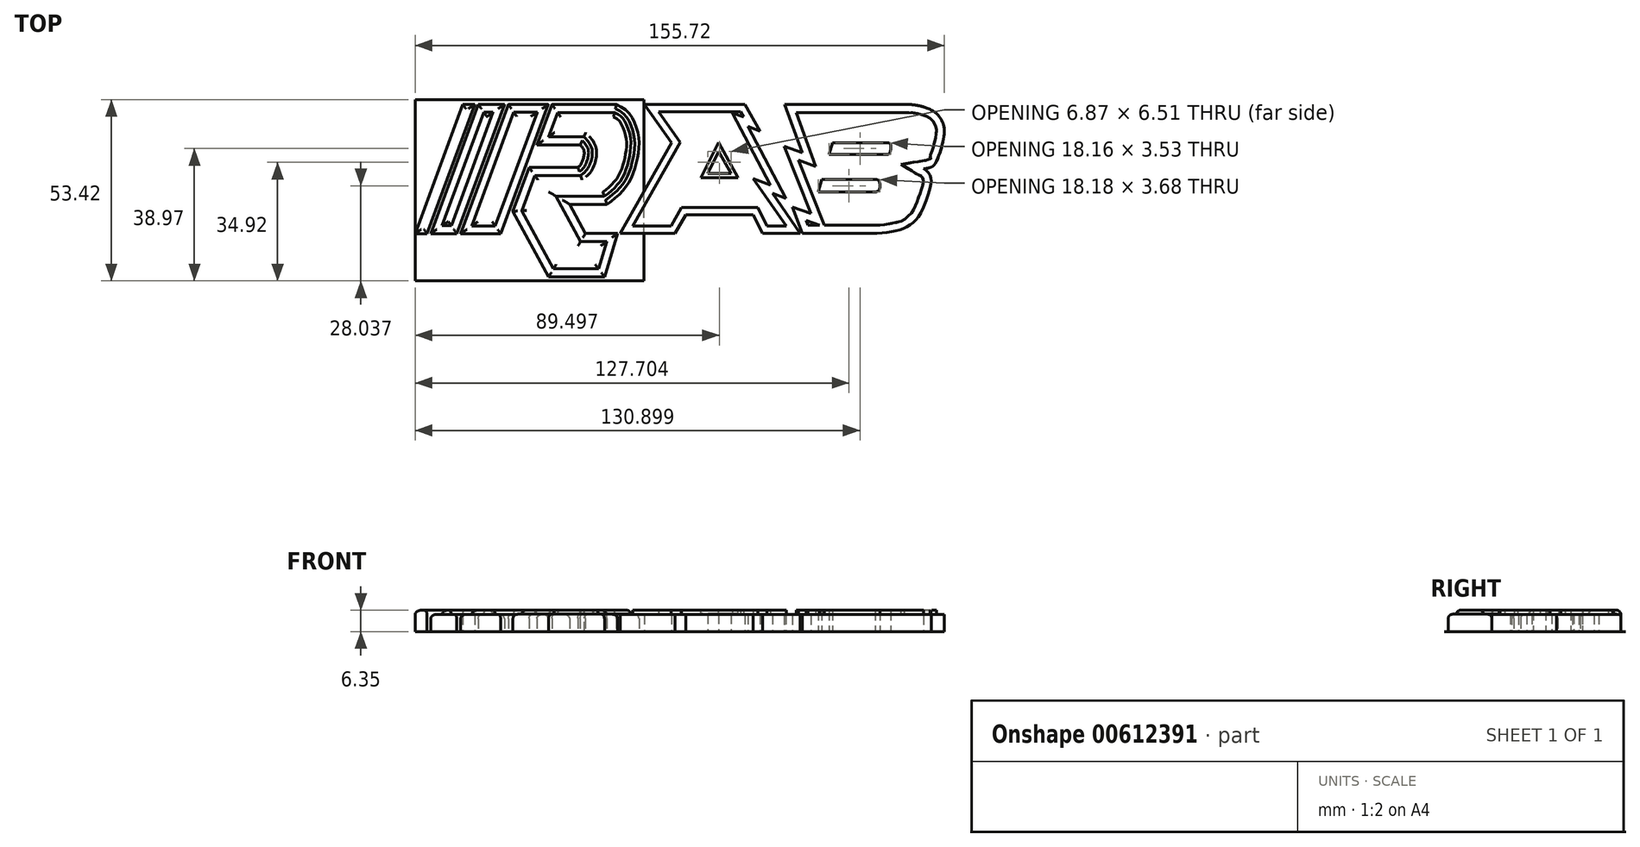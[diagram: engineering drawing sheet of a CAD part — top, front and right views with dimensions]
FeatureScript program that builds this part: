
annotation { "Feature Type Name" : "Feature", "Feature Type Description" : "" }
export const myFeature = defineFeature(function(context is Context, id is Id, definition is map)
    precondition{}
    {
        {
            var Q0;
            Q0=qCreatedBy(makeId("Top.planeOp"),FACE);
            var sketch = newSketch(context, id + "F0", { "sketchPlane" : qUnion([Q0])});
            skLineSegment(sketch, "E0", {"start": v(208.26, 38.07) * mm, "end": v(177.15, 38.07) * mm});
            skLineSegment(sketch, "E1", {"start": v(0, 0) * mm, "end": v(14, 38.07) * mm});
            skLineSegment(sketch, "E2", {"start": v(25.15, 0) * mm, "end": v(13.4, 0) * mm});
            skLineSegment(sketch, "E3", {"start": v(17.5, 38.07) * mm, "end": v(3.5, 0) * mm});
            skLineSegment(sketch, "E4", {"start": v(4.59, 0) * mm, "end": v(18.6, 38.07) * mm});
            skLineSegment(sketch, "E5", {"start": v(26.26, 38.07) * mm, "end": v(12.25, 0) * mm});
            skLineSegment(sketch, "E6", {"start": v(13.4, 0) * mm, "end": v(27.4, 38.07) * mm});
            skLineSegment(sketch, "E7", {"start": v(39.16, 38.07) * mm, "end": v(25.15, 0) * mm});
            skLineSegment(sketch, "E8", {"start": v(35.85, 26.18) * mm, "end": v(40.22, 38.07) * mm});
            skLineSegment(sketch, "E9", {"start": v(35.85, 26.18) * mm, "end": v(48.58, 26.18) * mm});
            skLineSegment(sketch, "E10", {"start": v(47.9, 19.52) * mm, "end": v(33.54, 19.52) * mm});
            skLineSegment(sketch, "E11", {"start": v(33.54, 19.52) * mm, "end": v(28.77, 6.57) * mm});
            skLineSegment(sketch, "E12", {"start": v(28.77, 6.57) * mm, "end": v(39.28, -12.73) * mm});
            skLineSegment(sketch, "E13", {"start": v(39.28, -12.73) * mm, "end": v(55.72, -12.73) * mm});
            skLineSegment(sketch, "E14", {"start": v(55.72, -12.73) * mm, "end": v(59.6, 0.09) * mm});
            skLineSegment(sketch, "E15", {"start": v(59.6, 0.09) * mm, "end": v(50.12, 0.09) * mm});
            skLineSegment(sketch, "E16", {"start": v(50.12, 0.09) * mm, "end": v(45.46, 8.65) * mm});
            skLineSegment(sketch, "E17", {"start": v(45.46, 8.65) * mm, "end": v(56.44, 8.65) * mm});
            skLineSegment(sketch, "E18", {"start": v(60.39, 0.09) * mm, "end": v(76.53, 0.09) * mm});
            skLineSegment(sketch, "E19", {"start": v(67.47, 38.07) * mm, "end": v(75.46, 26.74) * mm});
            skLineSegment(sketch, "E20", {"start": v(75.46, 26.74) * mm, "end": v(60.39, 0.09) * mm});
            skLineSegment(sketch, "E21", {"start": v(76.53, 0.09) * mm, "end": v(79.61, 5.54) * mm});
            skLineSegment(sketch, "E22", {"start": v(79.61, 5.54) * mm, "end": v(99.49, 5.54) * mm});
            skLineSegment(sketch, "E23", {"start": v(99.49, 5.54) * mm, "end": v(102.21, 0.09) * mm});
            skLineSegment(sketch, "E24", {"start": v(97.03, 38.07) * mm, "end": v(101.52, 30.22) * mm});
            skLineSegment(sketch, "E25", {"start": v(101.52, 30.22) * mm, "end": v(97.9, 31.58) * mm});
            skLineSegment(sketch, "E26", {"start": v(97.9, 31.58) * mm, "end": v(109.11, 10.42) * mm});
            skLineSegment(sketch, "E27", {"start": v(109.11, 10.42) * mm, "end": v(105.13, 11.87) * mm});
            skLineSegment(sketch, "E28", {"start": v(105.13, 11.87) * mm, "end": v(113.36, 0.09) * mm});
            skLineSegment(sketch, "E29", {"start": v(92.93, 17.75) * mm, "end": v(86.06, 17.75) * mm});
            skLineSegment(sketch, "E30", {"start": v(86.06, 17.75) * mm, "end": v(89.32, 24.25) * mm});
            skLineSegment(sketch, "E31", {"start": v(89.32, 24.25) * mm, "end": v(92.93, 17.75) * mm});
            skLineSegment(sketch, "E32", {"start": v(108.71, 38.07) * mm, "end": v(113.9, 23.8) * mm});
            skLineSegment(sketch, "E33", {"start": v(113.9, 23.8) * mm, "end": v(108.66, 25.8) * mm});
            skLineSegment(sketch, "E34", {"start": v(108.66, 25.8) * mm, "end": v(116.52, 5.9) * mm});
            skLineSegment(sketch, "E35", {"start": v(116.52, 5.9) * mm, "end": v(111, 7.9) * mm});
            skLineSegment(sketch, "E36", {"start": v(111, 7.9) * mm, "end": v(114, 0.09) * mm});
            skLineSegment(sketch, "E37", {"start": v(122.84, 26.81) * mm, "end": v(121.82, 23.29) * mm});
            skLineSegment(sketch, "E38", {"start": v(118.61, 12.28) * mm, "end": v(135.38, 12.28) * mm});
            skLineSegment(sketch, "E39", {"start": v(119.68, 15.96) * mm, "end": v(135.79, 15.96) * mm});
            skLineSegment(sketch, "E40", {"start": v(122.84, 26.81) * mm, "end": v(139.21, 26.81) * mm});
            skLineSegment(sketch, "E41", {"start": v(121.82, 23.29) * mm, "end": v(138.81, 23.29) * mm});
            skLineSegment(sketch, "E42", {"start": v(154.94, 38.07) * mm, "end": v(158.48, 30.05) * mm});
            skLineSegment(sketch, "E43", {"start": v(158.48, 30.05) * mm, "end": v(149.8, 0.09) * mm});
            skLineSegment(sketch, "E44", {"start": v(174.28, 38.07) * mm, "end": v(163.42, 0.09) * mm});
            skLineSegment(sketch, "E45", {"start": v(177.15, 38.07) * mm, "end": v(166.29, 0.09) * mm});
            skLineSegment(sketch, "E46", {"start": v(199.63, 25.83) * mm, "end": v(187.3, 25.83) * mm});
            skLineSegment(sketch, "E47", {"start": v(187.3, 25.83) * mm, "end": v(183.47, 12.44) * mm});
            skLineSegment(sketch, "E48", {"start": v(183.47, 12.44) * mm, "end": v(198.12, 12.44) * mm});
            skLineSegment(sketch, "E49", {"start": v(203.43, 21.85) * mm, "end": v(201.46, 14.99) * mm});
            skFitSpline(sketch, "E50", {"points": [v(219.55, 26.88) * mm, v(219.55, 31.52) * mm, v(217.56, 35.22) * mm, v(214.71, 36.84) * mm, v(208.26, 38.07) * mm], "startDerivative": vector(2.3, 18.78) * mm, "endDerivative": vector(-24.45, 0) * mm});
            skLineSegment(sketch, "E51", {"start": v(219.55, 26.88) * mm, "end": v(215.38, 11.32) * mm});
            skFitSpline(sketch, "E52", {"points": [v(149.65, 19.1) * mm, v(151.8, 19.57) * mm, v(153.28, 21.06) * mm, v(155.68, 29.22) * mm, v(155.1, 33.05) * mm, v(153.47, 35.33) * mm, v(150.12, 37.18) * mm, v(144.89, 38.07) * mm], "startDerivative": vector(20.2, 3.41) * mm, "endDerivative": vector(-28.09, 0) * mm});
            skFitSpline(sketch, "E53", {"points": [v(149.65, 19.1) * mm, v(151.02, 18) * mm, v(151.86, 16.02) * mm, v(151.72, 14.12) * mm, v(148.83, 6.08) * mm, v(146.58, 3.33) * mm, v(143.97, 1.57) * mm, v(140.72, 0.72) * mm, v(135.93, 0.09) * mm], "startDerivative": vector(16.43, -10.07) * mm, "endDerivative": vector(-33.98, 0) * mm});
            skFitSpline(sketch, "E54", {"points": [v(139.21, 26.81) * mm, v(139.63, 26.6) * mm, v(139.95, 26.07) * mm, v(139.77, 23.99) * mm, v(139.53, 23.54) * mm, v(138.81, 23.29) * mm], "startDerivative": vector(3.09, 0) * mm, "endDerivative": vector(-4.49, 0) * mm});
            skFitSpline(sketch, "E55", {"points": [v(135.79, 15.96) * mm, v(136.31, 15.73) * mm, v(136.7, 15.08) * mm, v(136.71, 13.28) * mm, v(136.38, 12.68) * mm, v(135.38, 12.28) * mm], "startDerivative": vector(3.73, 0) * mm, "endDerivative": vector(-8.7, -0.89) * mm});
            skFitSpline(sketch, "E56", {"points": [v(59.25, 38.07) * mm, v(62.12, 36.32) * mm, v(64.27, 33.3) * mm, v(65.78, 28.2) * mm, v(65.5, 22.76) * mm, v(63.84, 16.87) * mm, v(60.61, 12.07) * mm, v(56.44, 8.65) * mm], "startDerivative": vector(25.95, -13.02) * mm, "endDerivative": vector(-29.28, -21.25) * mm});
            skFitSpline(sketch, "E57", {"points": [v(199.63, 25.83) * mm, v(200.99, 25.52) * mm, v(202.05, 24.9) * mm, v(202.89, 23.96) * mm, v(203.43, 21.85) * mm], "startDerivative": vector(5.58, 0) * mm, "endDerivative": vector(-1.33, -10.82) * mm});
            skFitSpline(sketch, "E58", {"points": [v(198.12, 12.44) * mm, v(199.3, 12.72) * mm, v(200.4, 13.16) * mm, v(201.08, 13.97) * mm, v(201.46, 14.99) * mm], "startDerivative": vector(4.57, 1.01) * mm, "endDerivative": vector(1.33, 4.26) * mm});
            skLineSegment(sketch, "E59.trimOffspring", {"start": v(17.5, 38.07) * mm, "end": v(14, 38.07) * mm});
            skLineSegment(sketch, "E60.trimOffspring", {"start": v(26.26, 38.07) * mm, "end": v(18.6, 38.07) * mm});
            skLineSegment(sketch, "E61.trimOffspring", {"start": v(39.16, 38.07) * mm, "end": v(27.4, 38.07) * mm});
            skLineSegment(sketch, "E62.trimOffspring", {"start": v(59.25, 38.07) * mm, "end": v(40.22, 38.07) * mm});
            skLineSegment(sketch, "E63.trimOffspring", {"start": v(12.25, 0) * mm, "end": v(4.59, 0) * mm});
            skLineSegment(sketch, "E64.trimOffspring", {"start": v(3.5, 0) * mm, "end": v(0, 0) * mm});
            skLineSegment(sketch, "E65.trimOffspring", {"start": v(102.21, 0.09) * mm, "end": v(113.36, 0.09) * mm});
            skLineSegment(sketch, "E66.trimOffspring", {"start": v(114, 0.09) * mm, "end": v(135.93, 0.09) * mm});
            skLineSegment(sketch, "E67.trimOffspring", {"start": v(97.03, 38.07) * mm, "end": v(67.47, 38.07) * mm});
            skLineSegment(sketch, "E68.trimOffspring", {"start": v(119.68, 15.96) * mm, "end": v(118.61, 12.28) * mm});
            skLineSegment(sketch, "E69.trimOffspring", {"start": v(144.89, 38.07) * mm, "end": v(108.71, 38.07) * mm});
            skLineSegment(sketch, "E70.trimOffspring", {"start": v(149.8, 0.09) * mm, "end": v(163.42, 0.09) * mm});
            skLineSegment(sketch, "E71.trimOffspring", {"start": v(166.29, 0.09) * mm, "end": v(197.11, 0.09) * mm});
            skLineSegment(sketch, "E72.trimOffspring", {"start": v(174.28, 38.07) * mm, "end": v(154.94, 38.07) * mm});
            skFitSpline(sketch, "E73", {"points": [v(215.38, 11.32) * mm, v(214.17, 8.68) * mm, v(212.23, 5.94) * mm, v(209.39, 3.57) * mm, v(206.3, 1.9) * mm, v(202.66, 0.86) * mm, v(197.11, 0.09) * mm], "startDerivative": vector(-7.47, -18.05) * mm, "endDerivative": vector(-28.9, 0) * mm});
            skFitSpline(sketch, "E74", {"points": [v(48.58, 26.18) * mm, v(49.62, 24.65) * mm, v(49.56, 22.47) * mm, v(48.58, 20.18) * mm, v(47.9, 19.52) * mm], "startDerivative": vector(5.02, -5.67) * mm, "endDerivative": vector(-3.78, -2.78) * mm});
            skSolve(sketch);
        }
        {
            var Q0;
            Q0=makeQuery(id+"F0.imprint","IMPRINT",FACE,{"disambiguationData":[TD([[makeQuery(id+"F0.imprint","IMPRINT",EDGE,{"derivedFrom":sQuery(id+"F0.wireOp",EDGE,"E8")}),-1.0]])]});
            var Q1;
            Q1=makeQuery(id+"F0.imprint","IMPRINT",FACE,{"disambiguationData":[TD([[makeQuery(id+"F0.imprint","IMPRINT",EDGE,{"derivedFrom":sQuery(id+"F0.wireOp",EDGE,"E2")}),-1.0]])]});
            var Q2;
            Q2=makeQuery(id+"F0.imprint","IMPRINT",FACE,{"disambiguationData":[TD([[makeQuery(id+"F0.imprint","IMPRINT",EDGE,{"derivedFrom":sQuery(id+"F0.wireOp",EDGE,"E4")}),-1.0]])]});
            var Q3;
            Q3=makeQuery(id+"F0.imprint","IMPRINT",FACE,{"disambiguationData":[TD([[makeQuery(id+"F0.imprint","IMPRINT",EDGE,{"derivedFrom":sQuery(id+"F0.wireOp",EDGE,"E1")}),-1.0]])]});
            extrude(context, id + "F1", {"entities" : qUnion([Q0, Q1, Q2, Q3]), "depth" : 6.35 * mm, "offsetDistance" : 25.4 * mm});
        }
        {
            var Q0;
            Q0=qCreatedBy(makeId("Front.planeOp"),FACE);
            cPlane(context, id + "F2", {"entities" : qUnion([Q0]), "cplaneType" : CPlaneType.OFFSET, "offset" : 25.4 * mm, "oppositeDirection" : true, "width" : 152.4 * mm, "height" : 152.4 * mm});
        }
        {
            var Q0;
            Q0=qCreatedBy(id+"F2.planeOp",FACE);
            var sketch = newSketch(context, id + "F3", { "sketchPlane" : qUnion([Q0])});
            skLineSegment(sketch, "E75", {"start": v(63.44, 6.43) * mm, "end": v(63.44, 5.16) * mm});
            skLineSegment(sketch, "E76", {"start": v(63.44, 5.16) * mm, "end": v(65.98, 5.16) * mm});
            skLineSegment(sketch, "E77", {"start": v(65.98, 5.16) * mm, "end": v(65.98, 6.43) * mm});
            skLineSegment(sketch, "E78", {"start": v(65.98, 6.43) * mm, "end": v(63.44, 6.43) * mm});
            skSolve(sketch);
        }
        {
            var Q0;
            Q0 = qSketchRegion(id + "F3", true);
            var Q1;
            Q1=makeQuery(id+"F1.opExtrude","CAP_EDGE",EDGE,{"disambiguationData":[OSD([sQuery(id+"F0.wireOp",EDGE,"E56")])],"isStart":false});
            var Q2;
            Q2=makeQuery(id+"F1.opExtrude","CAP_EDGE",EDGE,{"disambiguationData":[OSD([sQuery(id+"F0.wireOp",EDGE,"E17")])],"isStart":false});
            var Q3;
            Q3=makeQuery(id+"F1.opExtrude","CAP_EDGE",EDGE,{"disambiguationData":[OSD([sQuery(id+"F0.wireOp",EDGE,"E16")])],"isStart":false});
            var Q4;
            Q4=makeQuery(id+"F1.opExtrude","CAP_EDGE",EDGE,{"disambiguationData":[OSD([sQuery(id+"F0.wireOp",EDGE,"E15")])],"isStart":false});
            var Q5;
            Q5=makeQuery(id+"F1.opExtrude","CAP_EDGE",EDGE,{"disambiguationData":[OSD([sQuery(id+"F0.wireOp",EDGE,"E14")])],"isStart":false});
            var Q6;
            Q6=makeQuery(id+"F1.opExtrude","CAP_EDGE",EDGE,{"disambiguationData":[OSD([sQuery(id+"F0.wireOp",EDGE,"E13")])],"isStart":false});
            var Q7;
            Q7=makeQuery(id+"F1.opExtrude","CAP_EDGE",EDGE,{"disambiguationData":[OSD([sQuery(id+"F0.wireOp",EDGE,"E12")])],"isStart":false});
            var Q8;
            Q8=makeQuery(id+"F1.opExtrude","CAP_EDGE",EDGE,{"disambiguationData":[OSD([sQuery(id+"F0.wireOp",EDGE,"E11")])],"isStart":false});
            var Q9;
            Q9=makeQuery(id+"F1.opExtrude","CAP_EDGE",EDGE,{"disambiguationData":[OSD([sQuery(id+"F0.wireOp",EDGE,"E10")])],"isStart":false});
            var Q10;
            Q10=makeQuery(id+"F1.opExtrude","CAP_EDGE",EDGE,{"disambiguationData":[OSD([sQuery(id+"F0.wireOp",EDGE,"E74")])],"isStart":false});
            var Q11;
            Q11=makeQuery(id+"F1.opExtrude","CAP_EDGE",EDGE,{"disambiguationData":[OSD([sQuery(id+"F0.wireOp",EDGE,"E9")])],"isStart":false});
            var Q12;
            Q12=makeQuery(id+"F1.opExtrude","CAP_EDGE",EDGE,{"disambiguationData":[OSD([sQuery(id+"F0.wireOp",EDGE,"E8")])],"isStart":false});
            var Q13;
            Q13=makeQuery(id+"F1.opExtrude","CAP_EDGE",EDGE,{"disambiguationData":[OSD([sQuery(id+"F0.wireOp",EDGE,"E62.trimOffspring")])],"isStart":false});
            sweep(context, id + "F4", {"operationType" : NewBodyOperationType.REMOVE, "profiles" : qUnion([Q0]), "path" : qUnion([Q1, Q2, Q3, Q4, Q5, Q6, Q7, Q8, Q9, Q10, Q11, Q12, Q13])});
        }
        {
            var Q0;
            Q0=qCreatedBy(id+"F2.planeOp",FACE);
            var sketch = newSketch(context, id + "F5", { "sketchPlane" : qUnion([Q0])});
            skLineSegment(sketch, "E79", {"start": v(32.09, 6.42) * mm, "end": v(32.09, 5.16) * mm});
            skLineSegment(sketch, "E80", {"start": v(32.09, 5.16) * mm, "end": v(34.63, 5.16) * mm});
            skLineSegment(sketch, "E81", {"start": v(34.63, 5.16) * mm, "end": v(34.63, 6.42) * mm});
            skLineSegment(sketch, "E82", {"start": v(34.63, 6.42) * mm, "end": v(32.09, 6.42) * mm});
            skSolve(sketch);
        }
        {
            var Q0;
            Q0 = qSketchRegion(id + "F5", true);
            var Q1;
            Q1=makeQuery(id+"F1.opExtrude","CAP_EDGE",EDGE,{"disambiguationData":[OSD([sQuery(id+"F0.wireOp",EDGE,"E7")])],"isStart":false});
            var Q2;
            Q2=makeQuery(id+"F1.opExtrude","CAP_EDGE",EDGE,{"disambiguationData":[OSD([sQuery(id+"F0.wireOp",EDGE,"E2")])],"isStart":false});
            var Q3;
            Q3=makeQuery(id+"F1.opExtrude","CAP_EDGE",EDGE,{"disambiguationData":[OSD([sQuery(id+"F0.wireOp",EDGE,"E6")])],"isStart":false});
            var Q4;
            Q4=makeQuery(id+"F1.opExtrude","CAP_EDGE",EDGE,{"disambiguationData":[OSD([sQuery(id+"F0.wireOp",EDGE,"E61.trimOffspring")])],"isStart":false});
            sweep(context, id + "F6", {"operationType" : NewBodyOperationType.REMOVE, "profiles" : qUnion([Q0]), "path" : qUnion([Q1, Q2, Q3, Q4])});
        }
        {
            var Q0;
            Q0=qCreatedBy(id+"F2.planeOp",FACE);
            var sketch = newSketch(context, id + "F7", { "sketchPlane" : qUnion([Q0])});
            skLineSegment(sketch, "E83", {"start": v(19.13, 6.42) * mm, "end": v(19.13, 5.16) * mm});
            skLineSegment(sketch, "E84", {"start": v(19.13, 5.16) * mm, "end": v(21.67, 5.16) * mm});
            skLineSegment(sketch, "E85", {"start": v(21.67, 5.16) * mm, "end": v(21.67, 6.42) * mm});
            skLineSegment(sketch, "E86", {"start": v(21.67, 6.42) * mm, "end": v(19.13, 6.42) * mm});
            skSolve(sketch);
        }
        {
            var Q0;
            Q0 = qSketchRegion(id + "F7", true);
            var Q1;
            Q1=makeQuery(id+"F1.opExtrude","CAP_EDGE",EDGE,{"disambiguationData":[OSD([sQuery(id+"F0.wireOp",EDGE,"E5")])],"isStart":false});
            var Q2;
            Q2=makeQuery(id+"F1.opExtrude","CAP_EDGE",EDGE,{"disambiguationData":[OSD([sQuery(id+"F0.wireOp",EDGE,"E63.trimOffspring")])],"isStart":false});
            var Q3;
            Q3=makeQuery(id+"F1.opExtrude","CAP_EDGE",EDGE,{"disambiguationData":[OSD([sQuery(id+"F0.wireOp",EDGE,"E4")])],"isStart":false});
            var Q4;
            Q4=makeQuery(id+"F1.opExtrude","CAP_EDGE",EDGE,{"disambiguationData":[OSD([sQuery(id+"F0.wireOp",EDGE,"E60.trimOffspring")])],"isStart":false});
            sweep(context, id + "F8", {"operationType" : NewBodyOperationType.REMOVE, "profiles" : qUnion([Q0]), "path" : qUnion([Q1, Q2, Q3, Q4])});
        }
        {
            var Q0;
            {var subQ0=sQuery(id+"F0.wireOp",EDGE,"E56");Q0=makeQuery(id+"F4.boolean.opBoolean","INTERSECT",EDGE,{"derivedFrom":[makeQuery(id+"F1.opExtrude","CAP_FACE",FACE,{"disambiguationData":[OSD([sQuery(id+"F0.wireOp",EDGE,"E8"),sQuery(id+"F0.wireOp",EDGE,"E9"),sQuery(id+"F0.wireOp",EDGE,"E10"),sQuery(id+"F0.wireOp",EDGE,"E11"),sQuery(id+"F0.wireOp",EDGE,"E12"),sQuery(id+"F0.wireOp",EDGE,"E13"),sQuery(id+"F0.wireOp",EDGE,"E14"),sQuery(id+"F0.wireOp",EDGE,"E15"),sQuery(id+"F0.wireOp",EDGE,"E16"),sQuery(id+"F0.wireOp",EDGE,"E17"),subQ0,sQuery(id+"F0.wireOp",EDGE,"E62.trimOffspring"),sQuery(id+"F0.wireOp",EDGE,"E74")])],"isStart":false}),makeQuery(id+"F4.opSweep","SWEPT_FACE",FACE,{"disambiguationData":[OSD([subQ0,sQuery(id+"F3.wireOp",EDGE,"E75")])]})]});}
            var Q1;
            {var subQ0=sQuery(id+"F0.wireOp",EDGE,"E17");Q1=makeQuery(id+"F4.boolean.opBoolean","INTERSECT",EDGE,{"derivedFrom":[makeQuery(id+"F1.opExtrude","CAP_FACE",FACE,{"disambiguationData":[OSD([sQuery(id+"F0.wireOp",EDGE,"E8"),sQuery(id+"F0.wireOp",EDGE,"E9"),sQuery(id+"F0.wireOp",EDGE,"E10"),sQuery(id+"F0.wireOp",EDGE,"E11"),sQuery(id+"F0.wireOp",EDGE,"E12"),sQuery(id+"F0.wireOp",EDGE,"E13"),sQuery(id+"F0.wireOp",EDGE,"E14"),sQuery(id+"F0.wireOp",EDGE,"E15"),sQuery(id+"F0.wireOp",EDGE,"E16"),subQ0,sQuery(id+"F0.wireOp",EDGE,"E56"),sQuery(id+"F0.wireOp",EDGE,"E62.trimOffspring"),sQuery(id+"F0.wireOp",EDGE,"E74")])],"isStart":false}),makeQuery(id+"F4.opSweep","SWEPT_FACE",FACE,{"disambiguationData":[OSD([subQ0,sQuery(id+"F3.wireOp",EDGE,"E75")])]})]});}
            var Q2;
            {var subQ0=sQuery(id+"F0.wireOp",EDGE,"E16");Q2=makeQuery(id+"F4.boolean.opBoolean","INTERSECT",EDGE,{"derivedFrom":[makeQuery(id+"F1.opExtrude","CAP_FACE",FACE,{"disambiguationData":[OSD([sQuery(id+"F0.wireOp",EDGE,"E8"),sQuery(id+"F0.wireOp",EDGE,"E9"),sQuery(id+"F0.wireOp",EDGE,"E10"),sQuery(id+"F0.wireOp",EDGE,"E11"),sQuery(id+"F0.wireOp",EDGE,"E12"),sQuery(id+"F0.wireOp",EDGE,"E13"),sQuery(id+"F0.wireOp",EDGE,"E14"),sQuery(id+"F0.wireOp",EDGE,"E15"),subQ0,sQuery(id+"F0.wireOp",EDGE,"E17"),sQuery(id+"F0.wireOp",EDGE,"E56"),sQuery(id+"F0.wireOp",EDGE,"E62.trimOffspring"),sQuery(id+"F0.wireOp",EDGE,"E74")])],"isStart":false}),makeQuery(id+"F4.opSweep","SWEPT_FACE",FACE,{"disambiguationData":[OSD([subQ0,sQuery(id+"F3.wireOp",EDGE,"E75")])]})]});}
            var Q3;
            {var subQ0=sQuery(id+"F0.wireOp",EDGE,"E15");Q3=makeQuery(id+"F4.boolean.opBoolean","INTERSECT",EDGE,{"derivedFrom":[makeQuery(id+"F1.opExtrude","CAP_FACE",FACE,{"disambiguationData":[OSD([sQuery(id+"F0.wireOp",EDGE,"E8"),sQuery(id+"F0.wireOp",EDGE,"E9"),sQuery(id+"F0.wireOp",EDGE,"E10"),sQuery(id+"F0.wireOp",EDGE,"E11"),sQuery(id+"F0.wireOp",EDGE,"E12"),sQuery(id+"F0.wireOp",EDGE,"E13"),sQuery(id+"F0.wireOp",EDGE,"E14"),subQ0,sQuery(id+"F0.wireOp",EDGE,"E16"),sQuery(id+"F0.wireOp",EDGE,"E17"),sQuery(id+"F0.wireOp",EDGE,"E56"),sQuery(id+"F0.wireOp",EDGE,"E62.trimOffspring"),sQuery(id+"F0.wireOp",EDGE,"E74")])],"isStart":false}),makeQuery(id+"F4.opSweep","SWEPT_FACE",FACE,{"disambiguationData":[OSD([subQ0,sQuery(id+"F3.wireOp",EDGE,"E75")])]})]});}
            var Q4;
            {var subQ0=sQuery(id+"F0.wireOp",EDGE,"E14");Q4=makeQuery(id+"F4.boolean.opBoolean","INTERSECT",EDGE,{"derivedFrom":[makeQuery(id+"F1.opExtrude","CAP_FACE",FACE,{"disambiguationData":[OSD([sQuery(id+"F0.wireOp",EDGE,"E8"),sQuery(id+"F0.wireOp",EDGE,"E9"),sQuery(id+"F0.wireOp",EDGE,"E10"),sQuery(id+"F0.wireOp",EDGE,"E11"),sQuery(id+"F0.wireOp",EDGE,"E12"),sQuery(id+"F0.wireOp",EDGE,"E13"),subQ0,sQuery(id+"F0.wireOp",EDGE,"E15"),sQuery(id+"F0.wireOp",EDGE,"E16"),sQuery(id+"F0.wireOp",EDGE,"E17"),sQuery(id+"F0.wireOp",EDGE,"E56"),sQuery(id+"F0.wireOp",EDGE,"E62.trimOffspring"),sQuery(id+"F0.wireOp",EDGE,"E74")])],"isStart":false}),makeQuery(id+"F4.opSweep","SWEPT_FACE",FACE,{"disambiguationData":[OSD([subQ0,sQuery(id+"F3.wireOp",EDGE,"E75")])]})]});}
            var Q5;
            Q5=makeQuery(id+"F4.boolean.opBoolean","INTERSECT",EDGE,{"derivedFrom":[makeQuery(id+"F1.opExtrude","SWEPT_FACE",FACE,{"disambiguationData":[OSD([sQuery(id+"F0.wireOp",EDGE,"E13")])]}),makeQuery(id+"F4.opSweep","SWEPT_FACE",FACE,{"disambiguationData":[OSD([sQuery(id+"F0.wireOp",EDGE,"E17"),sQuery(id+"F3.wireOp",EDGE,"E76")])]})]});
            var Q6;
            Q6=makeQuery(id+"F4.boolean.opBoolean","INTERSECT",EDGE,{"derivedFrom":[makeQuery(id+"F1.opExtrude","SWEPT_FACE",FACE,{"disambiguationData":[OSD([sQuery(id+"F0.wireOp",EDGE,"E14")])]}),makeQuery(id+"F4.opSweep","SWEPT_FACE",FACE,{"disambiguationData":[OSD([sQuery(id+"F0.wireOp",EDGE,"E17"),sQuery(id+"F3.wireOp",EDGE,"E76")])]})]});
            var Q7;
            {var subQ0=sQuery(id+"F0.wireOp",EDGE,"E17");Q7=makeQuery(id+"F4.boolean.opBoolean","INTERSECT",EDGE,{"derivedFrom":[makeQuery(id+"F1.opExtrude","SWEPT_FACE",FACE,{"disambiguationData":[OSD([subQ0])]}),makeQuery(id+"F4.opSweep","SWEPT_FACE",FACE,{"disambiguationData":[OSD([subQ0,sQuery(id+"F3.wireOp",EDGE,"E76")])]})]});}
            var Q8;
            Q8=makeQuery(id+"F4.boolean.opBoolean","INTERSECT",EDGE,{"derivedFrom":[makeQuery(id+"F1.opExtrude","SWEPT_FACE",FACE,{"disambiguationData":[OSD([sQuery(id+"F0.wireOp",EDGE,"E16")])]}),makeQuery(id+"F4.opSweep","SWEPT_FACE",FACE,{"disambiguationData":[OSD([sQuery(id+"F0.wireOp",EDGE,"E17"),sQuery(id+"F3.wireOp",EDGE,"E76")])]})]});
            var Q9;
            Q9=makeQuery(id+"F4.boolean.opBoolean","INTERSECT",EDGE,{"derivedFrom":[makeQuery(id+"F1.opExtrude","SWEPT_FACE",FACE,{"disambiguationData":[OSD([sQuery(id+"F0.wireOp",EDGE,"E15")])]}),makeQuery(id+"F4.opSweep","SWEPT_FACE",FACE,{"disambiguationData":[OSD([sQuery(id+"F0.wireOp",EDGE,"E17"),sQuery(id+"F3.wireOp",EDGE,"E76")])]})]});
            var Q10;
            Q10=makeQuery(id+"F4.boolean.opBoolean","INTERSECT",EDGE,{"derivedFrom":[makeQuery(id+"F1.opExtrude","SWEPT_FACE",FACE,{"disambiguationData":[OSD([sQuery(id+"F0.wireOp",EDGE,"E56")])]}),makeQuery(id+"F4.opSweep","SWEPT_FACE",FACE,{"disambiguationData":[OSD([sQuery(id+"F0.wireOp",EDGE,"E17"),sQuery(id+"F3.wireOp",EDGE,"E76")])]})]});
            var Q11;
            {var subQ0=sQuery(id+"F0.wireOp",EDGE,"E13");Q11=makeQuery(id+"F4.boolean.opBoolean","INTERSECT",EDGE,{"derivedFrom":[makeQuery(id+"F1.opExtrude","CAP_FACE",FACE,{"disambiguationData":[OSD([sQuery(id+"F0.wireOp",EDGE,"E8"),sQuery(id+"F0.wireOp",EDGE,"E9"),sQuery(id+"F0.wireOp",EDGE,"E10"),sQuery(id+"F0.wireOp",EDGE,"E11"),sQuery(id+"F0.wireOp",EDGE,"E12"),subQ0,sQuery(id+"F0.wireOp",EDGE,"E14"),sQuery(id+"F0.wireOp",EDGE,"E15"),sQuery(id+"F0.wireOp",EDGE,"E16"),sQuery(id+"F0.wireOp",EDGE,"E17"),sQuery(id+"F0.wireOp",EDGE,"E56"),sQuery(id+"F0.wireOp",EDGE,"E62.trimOffspring"),sQuery(id+"F0.wireOp",EDGE,"E74")])],"isStart":false}),makeQuery(id+"F4.opSweep","SWEPT_FACE",FACE,{"disambiguationData":[OSD([subQ0,sQuery(id+"F3.wireOp",EDGE,"E75")])]})]});}
            var Q12;
            {var subQ0=sQuery(id+"F0.wireOp",EDGE,"E12");Q12=makeQuery(id+"F4.boolean.opBoolean","INTERSECT",EDGE,{"derivedFrom":[makeQuery(id+"F1.opExtrude","CAP_FACE",FACE,{"disambiguationData":[OSD([sQuery(id+"F0.wireOp",EDGE,"E8"),sQuery(id+"F0.wireOp",EDGE,"E9"),sQuery(id+"F0.wireOp",EDGE,"E10"),sQuery(id+"F0.wireOp",EDGE,"E11"),subQ0,sQuery(id+"F0.wireOp",EDGE,"E13"),sQuery(id+"F0.wireOp",EDGE,"E14"),sQuery(id+"F0.wireOp",EDGE,"E15"),sQuery(id+"F0.wireOp",EDGE,"E16"),sQuery(id+"F0.wireOp",EDGE,"E17"),sQuery(id+"F0.wireOp",EDGE,"E56"),sQuery(id+"F0.wireOp",EDGE,"E62.trimOffspring"),sQuery(id+"F0.wireOp",EDGE,"E74")])],"isStart":false}),makeQuery(id+"F4.opSweep","SWEPT_FACE",FACE,{"disambiguationData":[OSD([subQ0,sQuery(id+"F3.wireOp",EDGE,"E75")])]})]});}
            var Q13;
            Q13=makeQuery(id+"F4.boolean.opBoolean","INTERSECT",EDGE,{"derivedFrom":[makeQuery(id+"F1.opExtrude","SWEPT_FACE",FACE,{"disambiguationData":[OSD([sQuery(id+"F0.wireOp",EDGE,"E12")])]}),makeQuery(id+"F4.opSweep","SWEPT_FACE",FACE,{"disambiguationData":[OSD([sQuery(id+"F0.wireOp",EDGE,"E17"),sQuery(id+"F3.wireOp",EDGE,"E76")])]})]});
            var Q14;
            Q14=makeQuery(id+"F4.boolean.opBoolean","INTERSECT",EDGE,{"derivedFrom":[makeQuery(id+"F1.opExtrude","SWEPT_FACE",FACE,{"disambiguationData":[OSD([sQuery(id+"F0.wireOp",EDGE,"E11")])]}),makeQuery(id+"F4.opSweep","SWEPT_FACE",FACE,{"disambiguationData":[OSD([sQuery(id+"F0.wireOp",EDGE,"E17"),sQuery(id+"F3.wireOp",EDGE,"E76")])]})]});
            var Q15;
            Q15=makeQuery(id+"F4.boolean.opBoolean","INTERSECT",EDGE,{"derivedFrom":[makeQuery(id+"F1.opExtrude","SWEPT_FACE",FACE,{"disambiguationData":[OSD([sQuery(id+"F0.wireOp",EDGE,"E10")])]}),makeQuery(id+"F4.opSweep","SWEPT_FACE",FACE,{"disambiguationData":[OSD([sQuery(id+"F0.wireOp",EDGE,"E17"),sQuery(id+"F3.wireOp",EDGE,"E76")])]})]});
            var Q16;
            {var subQ0=sQuery(id+"F0.wireOp",EDGE,"E11");Q16=makeQuery(id+"F4.boolean.opBoolean","INTERSECT",EDGE,{"derivedFrom":[makeQuery(id+"F1.opExtrude","CAP_FACE",FACE,{"disambiguationData":[OSD([sQuery(id+"F0.wireOp",EDGE,"E8"),sQuery(id+"F0.wireOp",EDGE,"E9"),sQuery(id+"F0.wireOp",EDGE,"E10"),subQ0,sQuery(id+"F0.wireOp",EDGE,"E12"),sQuery(id+"F0.wireOp",EDGE,"E13"),sQuery(id+"F0.wireOp",EDGE,"E14"),sQuery(id+"F0.wireOp",EDGE,"E15"),sQuery(id+"F0.wireOp",EDGE,"E16"),sQuery(id+"F0.wireOp",EDGE,"E17"),sQuery(id+"F0.wireOp",EDGE,"E56"),sQuery(id+"F0.wireOp",EDGE,"E62.trimOffspring"),sQuery(id+"F0.wireOp",EDGE,"E74")])],"isStart":false}),makeQuery(id+"F4.opSweep","SWEPT_FACE",FACE,{"disambiguationData":[OSD([subQ0,sQuery(id+"F3.wireOp",EDGE,"E75")])]})]});}
            var Q17;
            {var subQ0=sQuery(id+"F0.wireOp",EDGE,"E10");Q17=makeQuery(id+"F4.boolean.opBoolean","INTERSECT",EDGE,{"derivedFrom":[makeQuery(id+"F1.opExtrude","CAP_FACE",FACE,{"disambiguationData":[OSD([sQuery(id+"F0.wireOp",EDGE,"E8"),sQuery(id+"F0.wireOp",EDGE,"E9"),subQ0,sQuery(id+"F0.wireOp",EDGE,"E11"),sQuery(id+"F0.wireOp",EDGE,"E12"),sQuery(id+"F0.wireOp",EDGE,"E13"),sQuery(id+"F0.wireOp",EDGE,"E14"),sQuery(id+"F0.wireOp",EDGE,"E15"),sQuery(id+"F0.wireOp",EDGE,"E16"),sQuery(id+"F0.wireOp",EDGE,"E17"),sQuery(id+"F0.wireOp",EDGE,"E56"),sQuery(id+"F0.wireOp",EDGE,"E62.trimOffspring"),sQuery(id+"F0.wireOp",EDGE,"E74")])],"isStart":false}),makeQuery(id+"F4.opSweep","SWEPT_FACE",FACE,{"disambiguationData":[OSD([subQ0,sQuery(id+"F3.wireOp",EDGE,"E75")])]})]});}
            var Q18;
            Q18=makeQuery(id+"F4.boolean.opBoolean","INTERSECT",EDGE,{"derivedFrom":[makeQuery(id+"F1.opExtrude","SWEPT_FACE",FACE,{"disambiguationData":[OSD([sQuery(id+"F0.wireOp",EDGE,"E74")])]}),makeQuery(id+"F4.opSweep","SWEPT_FACE",FACE,{"disambiguationData":[OSD([sQuery(id+"F0.wireOp",EDGE,"E17"),sQuery(id+"F3.wireOp",EDGE,"E76")])]})]});
            var Q19;
            {var subQ0=sQuery(id+"F0.wireOp",EDGE,"E74");Q19=makeQuery(id+"F4.boolean.opBoolean","INTERSECT",EDGE,{"derivedFrom":[makeQuery(id+"F1.opExtrude","CAP_FACE",FACE,{"disambiguationData":[OSD([sQuery(id+"F0.wireOp",EDGE,"E8"),sQuery(id+"F0.wireOp",EDGE,"E9"),sQuery(id+"F0.wireOp",EDGE,"E10"),sQuery(id+"F0.wireOp",EDGE,"E11"),sQuery(id+"F0.wireOp",EDGE,"E12"),sQuery(id+"F0.wireOp",EDGE,"E13"),sQuery(id+"F0.wireOp",EDGE,"E14"),sQuery(id+"F0.wireOp",EDGE,"E15"),sQuery(id+"F0.wireOp",EDGE,"E16"),sQuery(id+"F0.wireOp",EDGE,"E17"),sQuery(id+"F0.wireOp",EDGE,"E56"),sQuery(id+"F0.wireOp",EDGE,"E62.trimOffspring"),subQ0])],"isStart":false}),makeQuery(id+"F4.opSweep","SWEPT_FACE",FACE,{"disambiguationData":[OSD([subQ0,sQuery(id+"F3.wireOp",EDGE,"E75")])]})]});}
            var Q20;
            {var subQ0=sQuery(id+"F0.wireOp",EDGE,"E9");Q20=makeQuery(id+"F4.boolean.opBoolean","INTERSECT",EDGE,{"derivedFrom":[makeQuery(id+"F1.opExtrude","CAP_FACE",FACE,{"disambiguationData":[OSD([sQuery(id+"F0.wireOp",EDGE,"E8"),subQ0,sQuery(id+"F0.wireOp",EDGE,"E10"),sQuery(id+"F0.wireOp",EDGE,"E11"),sQuery(id+"F0.wireOp",EDGE,"E12"),sQuery(id+"F0.wireOp",EDGE,"E13"),sQuery(id+"F0.wireOp",EDGE,"E14"),sQuery(id+"F0.wireOp",EDGE,"E15"),sQuery(id+"F0.wireOp",EDGE,"E16"),sQuery(id+"F0.wireOp",EDGE,"E17"),sQuery(id+"F0.wireOp",EDGE,"E56"),sQuery(id+"F0.wireOp",EDGE,"E62.trimOffspring"),sQuery(id+"F0.wireOp",EDGE,"E74")])],"isStart":false}),makeQuery(id+"F4.opSweep","SWEPT_FACE",FACE,{"disambiguationData":[OSD([subQ0,sQuery(id+"F3.wireOp",EDGE,"E75")])]})]});}
            var Q21;
            Q21=makeQuery(id+"F4.boolean.opBoolean","INTERSECT",EDGE,{"derivedFrom":[makeQuery(id+"F1.opExtrude","SWEPT_FACE",FACE,{"disambiguationData":[OSD([sQuery(id+"F0.wireOp",EDGE,"E9")])]}),makeQuery(id+"F4.opSweep","SWEPT_FACE",FACE,{"disambiguationData":[OSD([sQuery(id+"F0.wireOp",EDGE,"E17"),sQuery(id+"F3.wireOp",EDGE,"E76")])]})]});
            var Q22;
            Q22=makeQuery(id+"F4.boolean.opBoolean","INTERSECT",EDGE,{"derivedFrom":[makeQuery(id+"F1.opExtrude","SWEPT_FACE",FACE,{"disambiguationData":[OSD([sQuery(id+"F0.wireOp",EDGE,"E8")])]}),makeQuery(id+"F4.opSweep","SWEPT_FACE",FACE,{"disambiguationData":[OSD([sQuery(id+"F0.wireOp",EDGE,"E17"),sQuery(id+"F3.wireOp",EDGE,"E76")])]})]});
            var Q23;
            {var subQ0=sQuery(id+"F0.wireOp",EDGE,"E62.trimOffspring");Q23=makeQuery(id+"F4.boolean.opBoolean","INTERSECT",EDGE,{"derivedFrom":[makeQuery(id+"F1.opExtrude","CAP_FACE",FACE,{"disambiguationData":[OSD([sQuery(id+"F0.wireOp",EDGE,"E8"),sQuery(id+"F0.wireOp",EDGE,"E9"),sQuery(id+"F0.wireOp",EDGE,"E10"),sQuery(id+"F0.wireOp",EDGE,"E11"),sQuery(id+"F0.wireOp",EDGE,"E12"),sQuery(id+"F0.wireOp",EDGE,"E13"),sQuery(id+"F0.wireOp",EDGE,"E14"),sQuery(id+"F0.wireOp",EDGE,"E15"),sQuery(id+"F0.wireOp",EDGE,"E16"),sQuery(id+"F0.wireOp",EDGE,"E17"),sQuery(id+"F0.wireOp",EDGE,"E56"),subQ0,sQuery(id+"F0.wireOp",EDGE,"E74")])],"isStart":false}),makeQuery(id+"F4.opSweep","SWEPT_FACE",FACE,{"disambiguationData":[OSD([subQ0,sQuery(id+"F3.wireOp",EDGE,"E75")])]})]});}
            var Q24;
            {var subQ0=sQuery(id+"F0.wireOp",EDGE,"E8");Q24=makeQuery(id+"F4.boolean.opBoolean","INTERSECT",EDGE,{"derivedFrom":[makeQuery(id+"F1.opExtrude","CAP_FACE",FACE,{"disambiguationData":[OSD([subQ0,sQuery(id+"F0.wireOp",EDGE,"E9"),sQuery(id+"F0.wireOp",EDGE,"E10"),sQuery(id+"F0.wireOp",EDGE,"E11"),sQuery(id+"F0.wireOp",EDGE,"E12"),sQuery(id+"F0.wireOp",EDGE,"E13"),sQuery(id+"F0.wireOp",EDGE,"E14"),sQuery(id+"F0.wireOp",EDGE,"E15"),sQuery(id+"F0.wireOp",EDGE,"E16"),sQuery(id+"F0.wireOp",EDGE,"E17"),sQuery(id+"F0.wireOp",EDGE,"E56"),sQuery(id+"F0.wireOp",EDGE,"E62.trimOffspring"),sQuery(id+"F0.wireOp",EDGE,"E74")])],"isStart":false}),makeQuery(id+"F4.opSweep","SWEPT_FACE",FACE,{"disambiguationData":[OSD([subQ0,sQuery(id+"F3.wireOp",EDGE,"E75")])]})]});}
            var Q25;
            Q25=makeQuery(id+"F4.boolean.opBoolean","INTERSECT",EDGE,{"derivedFrom":[makeQuery(id+"F1.opExtrude","SWEPT_FACE",FACE,{"disambiguationData":[OSD([sQuery(id+"F0.wireOp",EDGE,"E62.trimOffspring")])]}),makeQuery(id+"F4.opSweep","SWEPT_FACE",FACE,{"disambiguationData":[OSD([sQuery(id+"F0.wireOp",EDGE,"E17"),sQuery(id+"F3.wireOp",EDGE,"E76")])]})]});
            var Q26;
            {var subQ0=sQuery(id+"F0.wireOp",EDGE,"E7");Q26=makeQuery(id+"F6.boolean.opBoolean","INTERSECT",EDGE,{"derivedFrom":[makeQuery(id+"F1.opExtrude","CAP_FACE",FACE,{"disambiguationData":[OSD([sQuery(id+"F0.wireOp",EDGE,"E2"),sQuery(id+"F0.wireOp",EDGE,"E6"),subQ0,sQuery(id+"F0.wireOp",EDGE,"E61.trimOffspring")])],"isStart":false}),makeQuery(id+"F6.opSweep","SWEPT_FACE",FACE,{"disambiguationData":[OSD([subQ0,sQuery(id+"F5.wireOp",EDGE,"E79")])]})]});}
            var Q27;
            {var subQ0=sQuery(id+"F0.wireOp",EDGE,"E2");Q27=makeQuery(id+"F6.boolean.opBoolean","INTERSECT",EDGE,{"derivedFrom":[makeQuery(id+"F1.opExtrude","CAP_FACE",FACE,{"disambiguationData":[OSD([subQ0,sQuery(id+"F0.wireOp",EDGE,"E6"),sQuery(id+"F0.wireOp",EDGE,"E7"),sQuery(id+"F0.wireOp",EDGE,"E61.trimOffspring")])],"isStart":false}),makeQuery(id+"F6.opSweep","SWEPT_FACE",FACE,{"disambiguationData":[OSD([subQ0,sQuery(id+"F5.wireOp",EDGE,"E79")])]})]});}
            var Q28;
            {var subQ0=sQuery(id+"F0.wireOp",EDGE,"E6");Q28=makeQuery(id+"F6.boolean.opBoolean","INTERSECT",EDGE,{"derivedFrom":[makeQuery(id+"F1.opExtrude","CAP_FACE",FACE,{"disambiguationData":[OSD([sQuery(id+"F0.wireOp",EDGE,"E2"),subQ0,sQuery(id+"F0.wireOp",EDGE,"E7"),sQuery(id+"F0.wireOp",EDGE,"E61.trimOffspring")])],"isStart":false}),makeQuery(id+"F6.opSweep","SWEPT_FACE",FACE,{"disambiguationData":[OSD([subQ0,sQuery(id+"F5.wireOp",EDGE,"E79")])]})]});}
            var Q29;
            {var subQ0=sQuery(id+"F0.wireOp",EDGE,"E61.trimOffspring");Q29=makeQuery(id+"F6.boolean.opBoolean","INTERSECT",EDGE,{"derivedFrom":[makeQuery(id+"F1.opExtrude","CAP_FACE",FACE,{"disambiguationData":[OSD([sQuery(id+"F0.wireOp",EDGE,"E2"),sQuery(id+"F0.wireOp",EDGE,"E6"),sQuery(id+"F0.wireOp",EDGE,"E7"),subQ0])],"isStart":false}),makeQuery(id+"F6.opSweep","SWEPT_FACE",FACE,{"disambiguationData":[OSD([subQ0,sQuery(id+"F5.wireOp",EDGE,"E79")])]})]});}
            var Q30;
            Q30=makeQuery(id+"F6.boolean.opBoolean","INTERSECT",EDGE,{"derivedFrom":[makeQuery(id+"F1.opExtrude","SWEPT_FACE",FACE,{"disambiguationData":[OSD([sQuery(id+"F0.wireOp",EDGE,"E61.trimOffspring")])]}),makeQuery(id+"F6.opSweep","SWEPT_FACE",FACE,{"disambiguationData":[OSD([sQuery(id+"F0.wireOp",EDGE,"E2"),sQuery(id+"F5.wireOp",EDGE,"E80")])]})]});
            var Q31;
            Q31=makeQuery(id+"F6.boolean.opBoolean","INTERSECT",EDGE,{"derivedFrom":[makeQuery(id+"F1.opExtrude","SWEPT_FACE",FACE,{"disambiguationData":[OSD([sQuery(id+"F0.wireOp",EDGE,"E7")])]}),makeQuery(id+"F6.opSweep","SWEPT_FACE",FACE,{"disambiguationData":[OSD([sQuery(id+"F0.wireOp",EDGE,"E2"),sQuery(id+"F5.wireOp",EDGE,"E80")])]})]});
            var Q32;
            Q32=makeQuery(id+"F6.boolean.opBoolean","INTERSECT",EDGE,{"derivedFrom":[makeQuery(id+"F1.opExtrude","SWEPT_FACE",FACE,{"disambiguationData":[OSD([sQuery(id+"F0.wireOp",EDGE,"E6")])]}),makeQuery(id+"F6.opSweep","SWEPT_FACE",FACE,{"disambiguationData":[OSD([sQuery(id+"F0.wireOp",EDGE,"E2"),sQuery(id+"F5.wireOp",EDGE,"E80")])]})]});
            var Q33;
            {var subQ0=sQuery(id+"F0.wireOp",EDGE,"E2");Q33=makeQuery(id+"F6.boolean.opBoolean","INTERSECT",EDGE,{"derivedFrom":[makeQuery(id+"F1.opExtrude","SWEPT_FACE",FACE,{"disambiguationData":[OSD([subQ0])]}),makeQuery(id+"F6.opSweep","SWEPT_FACE",FACE,{"disambiguationData":[OSD([subQ0,sQuery(id+"F5.wireOp",EDGE,"E80")])]})]});}
            var Q34;
            {var subQ0=sQuery(id+"F0.wireOp",EDGE,"E5");Q34=makeQuery(id+"F8.boolean.opBoolean","INTERSECT",EDGE,{"derivedFrom":[makeQuery(id+"F1.opExtrude","CAP_FACE",FACE,{"disambiguationData":[OSD([sQuery(id+"F0.wireOp",EDGE,"E4"),subQ0,sQuery(id+"F0.wireOp",EDGE,"E60.trimOffspring"),sQuery(id+"F0.wireOp",EDGE,"E63.trimOffspring")])],"isStart":false}),makeQuery(id+"F8.opSweep","SWEPT_FACE",FACE,{"disambiguationData":[OSD([subQ0,sQuery(id+"F7.wireOp",EDGE,"E83")])]})]});}
            var Q35;
            Q35=makeQuery(id+"F8.boolean.opBoolean","INTERSECT",EDGE,{"derivedFrom":[makeQuery(id+"F1.opExtrude","SWEPT_FACE",FACE,{"disambiguationData":[OSD([sQuery(id+"F0.wireOp",EDGE,"E5")])]}),makeQuery(id+"F8.opSweep","SWEPT_FACE",FACE,{"disambiguationData":[OSD([sQuery(id+"F0.wireOp",EDGE,"E63.trimOffspring"),sQuery(id+"F7.wireOp",EDGE,"E84")])]})]});
            var Q36;
            {var subQ0=sQuery(id+"F0.wireOp",EDGE,"E63.trimOffspring");Q36=makeQuery(id+"F8.boolean.opBoolean","INTERSECT",EDGE,{"derivedFrom":[makeQuery(id+"F1.opExtrude","CAP_FACE",FACE,{"disambiguationData":[OSD([sQuery(id+"F0.wireOp",EDGE,"E4"),sQuery(id+"F0.wireOp",EDGE,"E5"),sQuery(id+"F0.wireOp",EDGE,"E60.trimOffspring"),subQ0])],"isStart":false}),makeQuery(id+"F8.opSweep","SWEPT_FACE",FACE,{"disambiguationData":[OSD([subQ0,sQuery(id+"F7.wireOp",EDGE,"E83")])]})]});}
            var Q37;
            {var subQ0=sQuery(id+"F0.wireOp",EDGE,"E63.trimOffspring");Q37=makeQuery(id+"F8.boolean.opBoolean","INTERSECT",EDGE,{"derivedFrom":[makeQuery(id+"F1.opExtrude","SWEPT_FACE",FACE,{"disambiguationData":[OSD([subQ0])]}),makeQuery(id+"F8.opSweep","SWEPT_FACE",FACE,{"disambiguationData":[OSD([subQ0,sQuery(id+"F7.wireOp",EDGE,"E84")])]})]});}
            var Q38;
            {var subQ0=sQuery(id+"F0.wireOp",EDGE,"E4");Q38=makeQuery(id+"F8.boolean.opBoolean","INTERSECT",EDGE,{"derivedFrom":[makeQuery(id+"F1.opExtrude","CAP_FACE",FACE,{"disambiguationData":[OSD([subQ0,sQuery(id+"F0.wireOp",EDGE,"E5"),sQuery(id+"F0.wireOp",EDGE,"E60.trimOffspring"),sQuery(id+"F0.wireOp",EDGE,"E63.trimOffspring")])],"isStart":false}),makeQuery(id+"F8.opSweep","SWEPT_FACE",FACE,{"disambiguationData":[OSD([subQ0,sQuery(id+"F7.wireOp",EDGE,"E83")])]})]});}
            var Q39;
            Q39=makeQuery(id+"F8.boolean.opBoolean","INTERSECT",EDGE,{"derivedFrom":[makeQuery(id+"F1.opExtrude","SWEPT_FACE",FACE,{"disambiguationData":[OSD([sQuery(id+"F0.wireOp",EDGE,"E4")])]}),makeQuery(id+"F8.opSweep","SWEPT_FACE",FACE,{"disambiguationData":[OSD([sQuery(id+"F0.wireOp",EDGE,"E63.trimOffspring"),sQuery(id+"F7.wireOp",EDGE,"E84")])]})]});
            var Q40;
            Q40=makeQuery(id+"F1.opExtrude","CAP_FACE",FACE,{"disambiguationData":[OSD([sQuery(id+"F0.wireOp",EDGE,"E4"),sQuery(id+"F0.wireOp",EDGE,"E5"),sQuery(id+"F0.wireOp",EDGE,"E60.trimOffspring"),sQuery(id+"F0.wireOp",EDGE,"E63.trimOffspring")])],"isStart":false});
            var Q41;
            Q41=makeQuery(id+"F8.boolean.opBoolean","INTERSECT",EDGE,{"derivedFrom":[makeQuery(id+"F1.opExtrude","SWEPT_FACE",FACE,{"disambiguationData":[OSD([sQuery(id+"F0.wireOp",EDGE,"E60.trimOffspring")])]}),makeQuery(id+"F8.opSweep","SWEPT_FACE",FACE,{"disambiguationData":[OSD([sQuery(id+"F0.wireOp",EDGE,"E63.trimOffspring"),sQuery(id+"F7.wireOp",EDGE,"E84")])]})]});
            var Q42;
            Q42=makeQuery(id+"F1.opExtrude","CAP_EDGE",EDGE,{"disambiguationData":[OSD([sQuery(id+"F0.wireOp",EDGE,"E3")])],"isStart":false});
            var Q43;
            Q43=makeQuery(id+"F1.opExtrude","CAP_EDGE",EDGE,{"disambiguationData":[OSD([sQuery(id+"F0.wireOp",EDGE,"E59.trimOffspring")])],"isStart":false});
            var Q44;
            Q44=makeQuery(id+"F1.opExtrude","CAP_EDGE",EDGE,{"disambiguationData":[OSD([sQuery(id+"F0.wireOp",EDGE,"E1")])],"isStart":false});
            var Q45;
            Q45=makeQuery(id+"F1.opExtrude","CAP_EDGE",EDGE,{"disambiguationData":[OSD([sQuery(id+"F0.wireOp",EDGE,"E64.trimOffspring")])],"isStart":false});
            fillet(context, id + "F9", {"entities" : qUnion([Q0, Q1, Q2, Q3, Q4, Q5, Q6, Q7, Q8, Q9, Q10, Q11, Q12, Q13, Q14, Q15, Q16, Q17, Q18, Q19, Q20, Q21, Q22, Q23, Q24, Q25, Q26, Q27, Q28, Q29, Q30, Q31, Q32, Q33, Q34, Q35, Q36, Q37, Q38, Q39, Q40, Q41, Q42, Q43, Q44, Q45]), "radius" : 1.27 * mm, "tangentPropagation" : true, "allowEdgeOverflow" : false});
        }
        {
            var Q0;
            Q0=qCreatedBy(makeId("Top.planeOp"),FACE);
            var sketch = newSketch(context, id + "F10", { "sketchPlane" : qUnion([Q0])});
            skLineSegment(sketch, "E87.bottom", {"start": v(0, -13.92) * mm, "end": v(67.33, -13.92) * mm});
            skLineSegment(sketch, "E87.top", {"start": v(0, 39.5) * mm, "end": v(67.33, 39.5) * mm});
            skLineSegment(sketch, "E87.left", {"start": v(0, -13.92) * mm, "end": v(0, 39.5) * mm});
            skLineSegment(sketch, "E87.right", {"start": v(67.33, -13.92) * mm, "end": v(67.33, 39.5) * mm});
            skSolve(sketch);
        }
        {
            var Q0;
            Q0 = qSketchRegion(id + "F10", true);
            extrude(context, id + "F11", {"entities" : qUnion([Q0]), "depth" : 0 * mm, "offsetDistance" : 25.4 * mm});
        }
        {
            var Q0;
            Q0=makeQuery(id+"F0.imprint","IMPRINT",FACE,{"disambiguationData":[TD([[makeQuery(id+"F0.imprint","IMPRINT",EDGE,{"derivedFrom":sQuery(id+"F0.wireOp",EDGE,"E18")}),1.0]])]});
            var Q1;
            Q1=makeQuery(id+"F0.imprint","IMPRINT",FACE,{"disambiguationData":[TD([[makeQuery(id+"F0.imprint","IMPRINT",EDGE,{"derivedFrom":sQuery(id+"F0.wireOp",EDGE,"E32")}),1.0]])]});
            extrude(context, id + "F12", {"entities" : qUnion([Q0, Q1]), "depth" : 6.35 * mm, "offsetDistance" : 25.4 * mm});
        }
        {
            var Q0;
            Q0=qCreatedBy(id+"F2.planeOp",FACE);
            var sketch = newSketch(context, id + "F13", { "sketchPlane" : qUnion([Q0])});
            skLineSegment(sketch, "E88", {"start": v(74.64, 6.39) * mm, "end": v(74.64, 5.12) * mm});
            skLineSegment(sketch, "E89", {"start": v(74.64, 5.12) * mm, "end": v(77.18, 5.12) * mm});
            skLineSegment(sketch, "E90", {"start": v(77.18, 5.12) * mm, "end": v(77.18, 6.39) * mm});
            skLineSegment(sketch, "E91", {"start": v(77.18, 6.39) * mm, "end": v(74.64, 6.39) * mm});
            skSolve(sketch);
        }
        {
            var Q0;
            Q0 = qSketchRegion(id + "F13", true);
            var Q1;
            Q1=makeQuery(id+"F12.opExtrude","CAP_EDGE",EDGE,{"disambiguationData":[OSD([sQuery(id+"F0.wireOp",EDGE,"E20")])],"isStart":false});
            var Q2;
            Q2=makeQuery(id+"F12.opExtrude","CAP_EDGE",EDGE,{"disambiguationData":[OSD([sQuery(id+"F0.wireOp",EDGE,"E19")])],"isStart":false});
            var Q3;
            Q3=makeQuery(id+"F12.opExtrude","CAP_EDGE",EDGE,{"disambiguationData":[OSD([sQuery(id+"F0.wireOp",EDGE,"E18")])],"isStart":false});
            var Q4;
            Q4=makeQuery(id+"F12.opExtrude","CAP_EDGE",EDGE,{"disambiguationData":[OSD([sQuery(id+"F0.wireOp",EDGE,"E21")])],"isStart":false});
            var Q5;
            Q5=makeQuery(id+"F12.opExtrude","CAP_EDGE",EDGE,{"disambiguationData":[OSD([sQuery(id+"F0.wireOp",EDGE,"E22")])],"isStart":false});
            var Q6;
            Q6=makeQuery(id+"F12.opExtrude","CAP_EDGE",EDGE,{"disambiguationData":[OSD([sQuery(id+"F0.wireOp",EDGE,"E23")])],"isStart":false});
            var Q7;
            Q7=makeQuery(id+"F12.opExtrude","CAP_EDGE",EDGE,{"disambiguationData":[OSD([sQuery(id+"F0.wireOp",EDGE,"E65.trimOffspring")])],"isStart":false});
            var Q8;
            Q8=makeQuery(id+"F12.opExtrude","CAP_EDGE",EDGE,{"disambiguationData":[OSD([sQuery(id+"F0.wireOp",EDGE,"E28")])],"isStart":false});
            var Q9;
            Q9=makeQuery(id+"F12.opExtrude","CAP_EDGE",EDGE,{"disambiguationData":[OSD([sQuery(id+"F0.wireOp",EDGE,"E27")])],"isStart":false});
            var Q10;
            Q10=makeQuery(id+"F12.opExtrude","CAP_EDGE",EDGE,{"disambiguationData":[OSD([sQuery(id+"F0.wireOp",EDGE,"E26")])],"isStart":false});
            var Q11;
            Q11=makeQuery(id+"F12.opExtrude","CAP_EDGE",EDGE,{"disambiguationData":[OSD([sQuery(id+"F0.wireOp",EDGE,"E25")])],"isStart":false});
            var Q12;
            Q12=makeQuery(id+"F12.opExtrude","CAP_EDGE",EDGE,{"disambiguationData":[OSD([sQuery(id+"F0.wireOp",EDGE,"E24")])],"isStart":false});
            var Q13;
            Q13=makeQuery(id+"F12.opExtrude","CAP_EDGE",EDGE,{"disambiguationData":[OSD([sQuery(id+"F0.wireOp",EDGE,"E67.trimOffspring")])],"isStart":false});
            sweep(context, id + "F14", {"operationType" : NewBodyOperationType.REMOVE, "profiles" : qUnion([Q0]), "path" : qUnion([Q1, Q2, Q3, Q4, Q5, Q6, Q7, Q8, Q9, Q10, Q11, Q12, Q13])});
        }
        {
            var Q0;
            Q0=qCreatedBy(id+"F2.planeOp",FACE);
            var sketch = newSketch(context, id + "F15", { "sketchPlane" : qUnion([Q0])});
            skLineSegment(sketch, "E92", {"start": v(88.5, 6.6) * mm, "end": v(88.5, 5.33) * mm});
            skLineSegment(sketch, "E93", {"start": v(88.5, 5.33) * mm, "end": v(91.04, 5.33) * mm});
            skLineSegment(sketch, "E94", {"start": v(91.04, 5.33) * mm, "end": v(91.04, 6.6) * mm});
            skLineSegment(sketch, "E95", {"start": v(91.04, 6.6) * mm, "end": v(88.5, 6.6) * mm});
            skSolve(sketch);
        }
        {
            var Q0;
            Q0 = qSketchRegion(id + "F15", true);
            var Q1;
            Q1=makeQuery(id+"F12.opExtrude","CAP_EDGE",EDGE,{"disambiguationData":[OSD([sQuery(id+"F0.wireOp",EDGE,"E31")])],"isStart":false});
            var Q2;
            Q2=makeQuery(id+"F12.opExtrude","CAP_EDGE",EDGE,{"disambiguationData":[OSD([sQuery(id+"F0.wireOp",EDGE,"E29")])],"isStart":false});
            var Q3;
            Q3=makeQuery(id+"F12.opExtrude","CAP_EDGE",EDGE,{"disambiguationData":[OSD([sQuery(id+"F0.wireOp",EDGE,"E30")])],"isStart":false});
            sweep(context, id + "F16", {"operationType" : NewBodyOperationType.REMOVE, "profiles" : qUnion([Q0]), "path" : qUnion([Q1, Q2, Q3])});
        }
        {
            var Q0;
            Q0=qCreatedBy(id+"F2.planeOp",FACE);
            var sketch = newSketch(context, id + "F17", { "sketchPlane" : qUnion([Q0])});
            skLineSegment(sketch, "E96", {"start": v(113.3, 6.36) * mm, "end": v(113.3, 5.1) * mm});
            skLineSegment(sketch, "E97", {"start": v(113.3, 5.1) * mm, "end": v(115.85, 5.1) * mm});
            skLineSegment(sketch, "E98", {"start": v(115.85, 5.1) * mm, "end": v(115.85, 6.36) * mm});
            skLineSegment(sketch, "E99", {"start": v(115.85, 6.36) * mm, "end": v(113.3, 6.36) * mm});
            skSolve(sketch);
        }
        {
            var Q0;
            Q0 = qSketchRegion(id + "F17", true);
            var Q1;
            Q1 = qConstructionFilter(qBodyType(qCreatedBy(id + "F17" ,EDGE), BodyType.WIRE), ConstructionObject.NO);
            var Q2;
            Q2=makeQuery(id+"F12.opExtrude","CAP_EDGE",EDGE,{"disambiguationData":[OSD([sQuery(id+"F0.wireOp",EDGE,"E32")])],"isStart":false});
            var Q3;
            Q3=makeQuery(id+"F12.opExtrude","CAP_EDGE",EDGE,{"disambiguationData":[OSD([sQuery(id+"F0.wireOp",EDGE,"E33")])],"isStart":false});
            var Q4;
            Q4=makeQuery(id+"F12.opExtrude","CAP_EDGE",EDGE,{"disambiguationData":[OSD([sQuery(id+"F0.wireOp",EDGE,"E34")])],"isStart":false});
            var Q5;
            Q5=makeQuery(id+"F12.opExtrude","CAP_EDGE",EDGE,{"disambiguationData":[OSD([sQuery(id+"F0.wireOp",EDGE,"E35")])],"isStart":false});
            var Q6;
            Q6=makeQuery(id+"F12.opExtrude","CAP_EDGE",EDGE,{"disambiguationData":[OSD([sQuery(id+"F0.wireOp",EDGE,"E36")])],"isStart":false});
            var Q7;
            Q7=makeQuery(id+"F12.opExtrude","CAP_EDGE",EDGE,{"disambiguationData":[OSD([sQuery(id+"F0.wireOp",EDGE,"E66.trimOffspring")])],"isStart":false});
            var Q8;
            Q8=makeQuery(id+"F12.opExtrude","CAP_EDGE",EDGE,{"disambiguationData":[OSD([sQuery(id+"F0.wireOp",EDGE,"E69.trimOffspring")])],"isStart":false});
            var Q9;
            Q9=makeQuery(id+"F12.opExtrude","CAP_EDGE",EDGE,{"disambiguationData":[OSD([sQuery(id+"F0.wireOp",EDGE,"E52")])],"isStart":false});
            var Q10;
            Q10=makeQuery(id+"F12.opExtrude","CAP_EDGE",EDGE,{"disambiguationData":[OSD([sQuery(id+"F0.wireOp",EDGE,"E53")])],"isStart":false});
            sweep(context, id + "F18", {"operationType" : NewBodyOperationType.REMOVE, "profiles" : qUnion([Q0]), "surfaceProfiles" : qUnion([Q1]), "path" : qUnion([Q2, Q3, Q4, Q5, Q6, Q7, Q8, Q9, Q10])});
        }
    });
